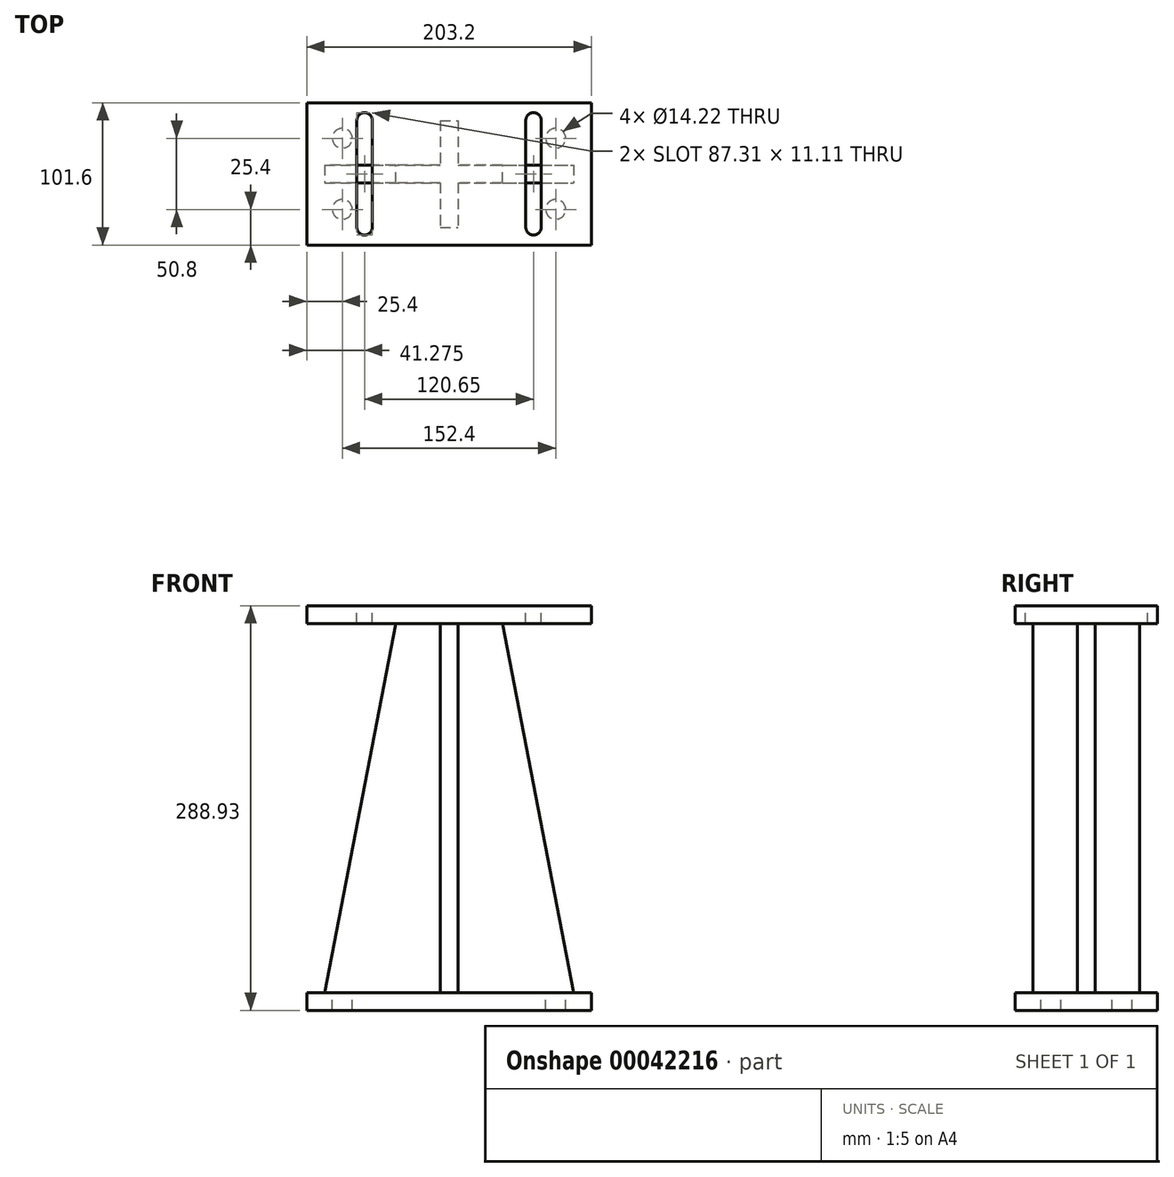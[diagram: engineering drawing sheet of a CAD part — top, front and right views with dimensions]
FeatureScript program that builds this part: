
annotation { "Feature Type Name" : "Feature", "Feature Type Description" : "" }
export const myFeature = defineFeature(function(context is Context, id is Id, definition is map)
    precondition{}
    {
        {
            var Q0;
            Q0=qCreatedBy(makeId("Top.planeOp"),FACE);
            var sketch = newSketch(context, id + "F0", { "sketchPlane" : qUnion([Q0])});
            skLineSegment(sketch, "E0.rect.bottom", {"start": v(-101.6, 50.8) * mm, "end": v(101.6, 50.8) * mm});
            skLineSegment(sketch, "E0.rect.top", {"start": v(-101.6, -50.8) * mm, "end": v(101.6, -50.8) * mm});
            skLineSegment(sketch, "E0.rect.left", {"start": v(-101.6, 50.8) * mm, "end": v(-101.6, -50.8) * mm});
            skLineSegment(sketch, "E0.rect.right", {"start": v(101.6, 50.8) * mm, "end": v(101.6, -50.8) * mm});
            skPoint(sketch, "E0.rect.middle", {"position": v(0, 0) * mm});
            skLineSegment(sketch, "E1.0", {"start": v(-76.2, 25.4) * mm, "end": v(76.2, 25.4) * mm, "construction": true});
            skLineSegment(sketch, "E1.1", {"start": v(-76.2, 25.4) * mm, "end": v(-76.2, -25.4) * mm, "construction": true});
            skLineSegment(sketch, "E1.2", {"start": v(-76.2, -25.4) * mm, "end": v(76.2, -25.4) * mm, "construction": true});
            skLineSegment(sketch, "E1.3", {"start": v(76.2, 25.4) * mm, "end": v(76.2, -25.4) * mm, "construction": true});
            skPoint(sketch, "E2", {"position": v(-76.2, 25.4) * mm});
            skPoint(sketch, "E3", {"position": v(76.2, 25.4) * mm});
            skPoint(sketch, "E4", {"position": v(76.2, -25.4) * mm});
            skPoint(sketch, "E5", {"position": v(-76.2, -25.4) * mm});
            skSolve(sketch);
        }
        {
            var Q0;
            Q0=qSketchRegion(id+"F0",true);
            extrude(context, id + "F1", {"entities" : qUnion([Q0]), "oppositeDirection" : true, "depth" : 12.7 * mm});
        }
        {
            var Q0;
            Q0=sQuery(id+"F0.wireOp",VERTEX,"E2");
            var Q1;
            Q1=sQuery(id+"F0.wireOp",VERTEX,"E3");
            var Q2;
            Q2=sQuery(id+"F0.wireOp",VERTEX,"E4");
            var Q3;
            Q3=sQuery(id+"F0.wireOp",VERTEX,"E5");
            var Q4;
            Q4=makeQuery(id+"F1.opExtrude","SWEPT_BODY",BODY,{"disambiguationData":[OSD([sQuery(id+"F0.wireOp",EDGE,"E0.rect.bottom"),sQuery(id+"F0.wireOp",EDGE,"E0.rect.top"),sQuery(id+"F0.wireOp",EDGE,"E0.rect.left"),sQuery(id+"F0.wireOp",EDGE,"E0.rect.right")])]});
            hole(context, id + "F2", {"style" : HoleStyle.SIMPLE, "holeDiameter" : 14.22 * mm, "endStyle" : HoleEndStyle.THROUGH, "locations" : qUnion([Q0, Q1, Q2, Q3]), "scope" : qUnion([Q4])});
        }
        {
            var Q0;
            Q0=makeQuery(id+"F1.opExtrude","CAP_FACE",FACE,{"disambiguationData":[OSD([sQuery(id+"F0.wireOp",EDGE,"E0.rect.bottom"),sQuery(id+"F0.wireOp",EDGE,"E0.rect.top"),sQuery(id+"F0.wireOp",EDGE,"E0.rect.left"),sQuery(id+"F0.wireOp",EDGE,"E0.rect.right")])],"isStart":false});
            cPlane(context, id + "F3", {"entities" : qUnion([Q0]), "cplaneType" : CPlaneType.OFFSET, "offset" : 288.93 * mm, "oppositeDirection" : true, "width" : 152.4 * mm, "height" : 152.4 * mm});
        }
        {
            var Q0;
            Q0=qCreatedBy(id+"F3.planeOp",FACE);
            var sketch = newSketch(context, id + "F4", { "sketchPlane" : qUnion([Q0])});
            skLineSegment(sketch, "E6.0", {"start": v(-101.6, -50.8) * mm, "end": v(101.6, -50.8) * mm});
            skLineSegment(sketch, "E7.0", {"start": v(101.6, -50.8) * mm, "end": v(101.6, 50.8) * mm});
            skLineSegment(sketch, "E8.0", {"start": v(-101.6, 50.8) * mm, "end": v(101.6, 50.8) * mm});
            skLineSegment(sketch, "E9.0", {"start": v(-101.6, -50.8) * mm, "end": v(-101.6, 50.8) * mm});
            skSolve(sketch);
        }
        {
            var Q0;
            Q0=qSketchRegion(id+"F4",true);
            extrude(context, id + "F5", {"entities" : qUnion([Q0]), "depth" : 12.7 * mm});
        }
        {
            var Q0;
            Q0=makeQuery(id+"F0.imprint","IMPRINT",FACE,{"disambiguationData":[TD([[makeQuery(id+"F0.imprint","IMPRINT",EDGE,{"derivedFrom":sQuery(id+"F0.wireOp",EDGE,"E0.rect.bottom")}),-1.0]])]});
            var sketch = newSketch(context, id + "F6", { "sketchPlane" : qUnion([Q0])});
            skLineSegment(sketch, "E10.rect.bottom", {"start": v(-6.35, 38.1) * mm, "end": v(6.35, 38.1) * mm});
            skLineSegment(sketch, "E10.rect.top", {"start": v(-6.35, -38.1) * mm, "end": v(6.35, -38.1) * mm});
            skLineSegment(sketch, "E10.rect.left", {"start": v(-6.35, 38.1) * mm, "end": v(-6.35, -38.1) * mm});
            skLineSegment(sketch, "E10.rect.right", {"start": v(6.35, 38.1) * mm, "end": v(6.35, -38.1) * mm});
            skPoint(sketch, "E10.rect.middle", {"position": v(0, 0) * mm});
            skLineSegment(sketch, "E11.rect.bottom", {"start": v(-38.1, 6.35) * mm, "end": v(38.1, 6.35) * mm});
            skLineSegment(sketch, "E11.rect.top", {"start": v(-38.1, -6.35) * mm, "end": v(38.1, -6.35) * mm});
            skLineSegment(sketch, "E11.rect.left", {"start": v(-38.1, 6.35) * mm, "end": v(-38.1, -6.35) * mm});
            skLineSegment(sketch, "E11.rect.right", {"start": v(38.1, 6.35) * mm, "end": v(38.1, -6.35) * mm});
            skSolve(sketch);
        }
        {
            var Q0;
            Q0=qSketchRegion(id+"F6",true);
            var Q1;
            Q1=makeQuery(id+"F5.opExtrude","CAP_FACE",FACE,{"disambiguationData":[OSD([sQuery(id+"F4.wireOp",EDGE,"E6.0"),sQuery(id+"F4.wireOp",EDGE,"E7.0"),sQuery(id+"F4.wireOp",EDGE,"E8.0"),sQuery(id+"F4.wireOp",EDGE,"E9.0")])],"isStart":false});
            extrude(context, id + "F7", {"entities" : qUnion([Q0]), "endBound" : BoundingType.UP_TO_SURFACE, "endBoundEntityFace" : qUnion([Q1]), "depth" : 25.4 * mm});
        }
        {
            var Q0;
            Q0=makeQuery(id+"F5.opExtrude","CAP_FACE",FACE,{"disambiguationData":[OSD([sQuery(id+"F4.wireOp",EDGE,"E6.0"),sQuery(id+"F4.wireOp",EDGE,"E7.0"),sQuery(id+"F4.wireOp",EDGE,"E8.0"),sQuery(id+"F4.wireOp",EDGE,"E9.0")])],"isStart":true});
            var sketch = newSketch(context, id + "F8", { "sketchPlane" : qUnion([Q0])});
            skLineSegment(sketch, "E12", {"start": v(-101.6, 0) * mm, "end": v(101.6, 0) * mm, "construction": true});
            skLineSegment(sketch, "E13", {"start": v(0, 50.8) * mm, "end": v(0, -50.8) * mm, "construction": true});
            skLineSegment(sketch, "E14.0", {"start": v(-60.32, 76.2) * mm, "end": v(-60.33, -76.2) * mm, "construction": true});
            skLineSegment(sketch, "E15.0", {"start": v(-101.6, 19.81) * mm, "end": v(101.6, 19.81) * mm, "construction": true});
            skPoint(sketch, "E16", {"position": v(-60.32, 19.81) * mm});
            skPoint(sketch, "E17.MirrorP", {"position": v(-60.32, -19.81) * mm});
            skPoint(sketch, "E18.MirrorP", {"position": v(60.32, 19.81) * mm});
            skPoint(sketch, "E19.MirrorP", {"position": v(60.32, -19.81) * mm});
            skLineSegment(sketch, "E20", {"start": v(-60.32, 12.7) * mm, "end": v(-60.32, 38.1) * mm});
            skArc(sketch, "E21.0.startCap", {"start": v(-54.77, 12.7) * mm, "mid": v(-60.32, 7.14) * mm, "end": v(-65.88, 12.7) * mm});
            skArc(sketch, "E21.0.endCap", {"start": v(-65.88, 38.1) * mm, "mid": v(-60.33, 43.66) * mm, "end": v(-54.77, 38.1) * mm});
            skLineSegment(sketch, "E21.0.left", {"start": v(-65.88, 12.7) * mm, "end": v(-65.88, 38.1) * mm});
            skLineSegment(sketch, "E21.0.right", {"start": v(-54.77, -12.7) * mm, "end": v(-54.77, 38.1) * mm});
            skLineSegment(sketch, "E22.MirrorCS", {"start": v(-65.88, 12.7) * mm, "end": v(-65.88, -38.1) * mm});
            skLineSegment(sketch, "E23.MirrorCS", {"start": v(-54.77, -12.7) * mm, "end": v(-54.77, -38.1) * mm});
            skLineSegment(sketch, "E24.MirrorCS", {"start": v(-60.32, -12.7) * mm, "end": v(-60.32, -38.1) * mm});
            skArc(sketch, "E25.MirrorCS", {"start": v(-65.88, -38.1) * mm, "mid": v(-60.32, -43.66) * mm, "end": v(-54.77, -38.1) * mm});
            skArc(sketch, "E26.MirrorCS", {"start": v(-54.77, -12.7) * mm, "mid": v(-60.32, -7.14) * mm, "end": v(-65.88, -12.7) * mm});
            skArc(sketch, "E27.MirrorCS", {"start": v(54.77, -12.7) * mm, "mid": v(60.32, -7.14) * mm, "end": v(65.88, -12.7) * mm});
            skArc(sketch, "E28.MirrorCS", {"start": v(54.77, 12.7) * mm, "mid": v(60.33, 7.14) * mm, "end": v(65.88, 12.7) * mm});
            skLineSegment(sketch, "E29.MirrorCS", {"start": v(65.88, -12.7) * mm, "end": v(65.88, -38.1) * mm});
            skLineSegment(sketch, "E30.MirrorCS", {"start": v(60.32, 12.7) * mm, "end": v(60.33, 38.1) * mm});
            skArc(sketch, "E31.MirrorCS", {"start": v(65.88, -38.1) * mm, "mid": v(60.32, -43.66) * mm, "end": v(54.77, -38.1) * mm});
            skLineSegment(sketch, "E32.MirrorCS", {"start": v(54.77, -12.7) * mm, "end": v(54.77, -38.1) * mm});
            skLineSegment(sketch, "E33.MirrorCS", {"start": v(60.32, -12.7) * mm, "end": v(60.32, -38.1) * mm});
            skArc(sketch, "E34.MirrorCS", {"start": v(65.88, 38.1) * mm, "mid": v(60.32, 43.66) * mm, "end": v(54.77, 38.1) * mm});
            skLineSegment(sketch, "E35.MirrorCS", {"start": v(65.88, -12.7) * mm, "end": v(65.88, 38.1) * mm});
            skLineSegment(sketch, "E36.MirrorCS", {"start": v(54.77, -12.7) * mm, "end": v(54.77, 38.1) * mm});
            skSolve(sketch);
        }
        {
            var Q0;
            Q0=qSketchRegion(id+"F8",true);
            extrude(context, id + "F9", {"entities" : qUnion([Q0]), "operationType" : NewBodyOperationType.REMOVE, "oppositeDirection" : true, "depth" : 25.4 * mm});
        }
        {
            var Q0;
            {var subQ0=sQuery(id+"F6.wireOp",EDGE,"E11.rect.top");Q0=makeQuery(id+"F7.opExtrude","SWEPT_FACE",FACE,{"disambiguationData":[OSD([subQ0]),TDD([makeQuery(id+"F6.imprint","IMPRINT",EDGE,{"disambiguationData":[TD([[makeQuery(id+"F6.imprint","INTERSECT",VERTEX,{"derivedFrom":[subQ0,sQuery(id+"F6.wireOp",EDGE,"E11.rect.right")]}),1.0]])],"derivedFrom":subQ0})])]});}
            var sketch = newSketch(context, id + "F10", { "sketchPlane" : qUnion([Q0])});
            skLineSegment(sketch, "E37.0", {"start": v(38.1, 263.53) * mm, "end": v(38.1, 0) * mm});
            skLineSegment(sketch, "E38.0", {"start": v(-101.6, 0) * mm, "end": v(101.6, 0) * mm});
            skLineSegment(sketch, "E39", {"start": v(38.1, 263.53) * mm, "end": v(88.9, 0) * mm});
            skLineSegment(sketch, "E40", {"start": v(0, 353.21) * mm, "end": v(0, -98.5) * mm, "construction": true});
            skLineSegment(sketch, "E41.MirrorCS", {"start": v(-38.1, 263.53) * mm, "end": v(-38.1, 0) * mm});
            skLineSegment(sketch, "E42.MirrorCS", {"start": v(-38.1, 263.53) * mm, "end": v(-88.9, 0) * mm});
            skSolve(sketch);
        }
        {
            var Q0;
            Q0=qSketchRegion(id+"F10",true);
            extrude(context, id + "F11", {"entities" : qUnion([Q0]), "operationType" : NewBodyOperationType.ADD, "oppositeDirection" : true, "depth" : 12.7 * mm});
        }
    });
